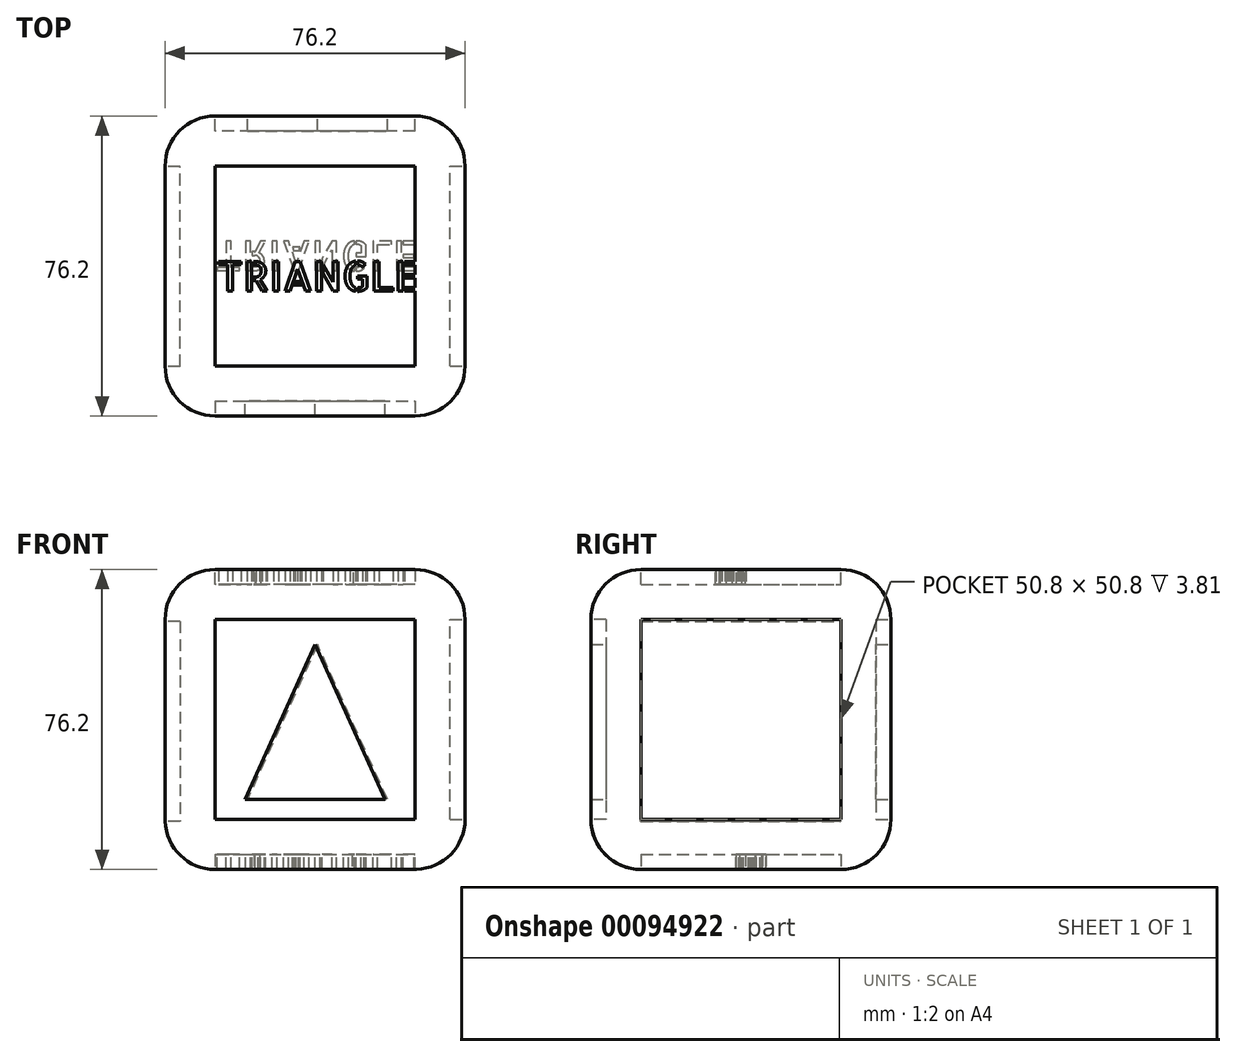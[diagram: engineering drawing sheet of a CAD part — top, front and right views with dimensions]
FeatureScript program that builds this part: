
annotation { "Feature Type Name" : "Feature", "Feature Type Description" : "" }
export const myFeature = defineFeature(function(context is Context, id is Id, definition is map)
    precondition{}
    {
        {
            var Q0;
            Q0=qCreatedBy(makeId("Front.planeOp"),FACE);
            var sketch = newSketch(context, id + "F0", { "sketchPlane" : qUnion([Q0])});
            skLineSegment(sketch, "E0", {"start": v(0, 0) * mm, "end": v(76.2, 0) * mm});
            skLineSegment(sketch, "E1", {"start": v(76.2, 0) * mm, "end": v(76.2, 76.2) * mm});
            skLineSegment(sketch, "E2", {"start": v(76.2, 76.2) * mm, "end": v(0, 76.2) * mm});
            skLineSegment(sketch, "E3", {"start": v(0, 76.2) * mm, "end": v(0, 0) * mm});
            skSolve(sketch);
        }
        {
            var Q0;
            Q0 = qSketchRegion(id + "F0", true);
            var Q1;
            Q1=makeQuery(id+"F0.imprint","IMPRINT",FACE,{"disambiguationData":[TD([[makeQuery(id+"F0.imprint","IMPRINT",EDGE,{"derivedFrom":sQuery(id+"F0.wireOp",EDGE,"E0")}),1.0]])]});
            extrude(context, id + "F1", {"entities" : qUnion([Q0, Q1]), "depth" : 76.2 * mm});
        }
        {
            var Q0;
            Q0=makeQuery(id+"F1.opExtrude","CAP_EDGE",EDGE,{"disambiguationData":[OSD([sQuery(id+"F0.wireOp",EDGE,"E1")])],"isStart":false});
            var Q1;
            Q1=makeQuery(id+"F1.opExtrude","CAP_EDGE",EDGE,{"disambiguationData":[OSD([sQuery(id+"F0.wireOp",EDGE,"E2")])],"isStart":false});
            var Q2;
            Q2=makeQuery(id+"F1.opExtrude","CAP_EDGE",EDGE,{"disambiguationData":[OSD([sQuery(id+"F0.wireOp",EDGE,"E3")])],"isStart":false});
            var Q3;
            Q3=makeQuery(id+"F1.opExtrude","CAP_EDGE",EDGE,{"disambiguationData":[OSD([sQuery(id+"F0.wireOp",EDGE,"E0")])],"isStart":false});
            var Q4;
            Q4=makeQuery(id+"F1.opExtrude","SWEPT_EDGE",EDGE,{"disambiguationData":[OSD([sQuery(id+"F0.wireOp",EDGE,"E0"),sQuery(id+"F0.wireOp",EDGE,"E1")])]});
            var Q5;
            Q5=makeQuery(id+"F1.opExtrude","SWEPT_EDGE",EDGE,{"disambiguationData":[OSD([sQuery(id+"F0.wireOp",EDGE,"E1"),sQuery(id+"F0.wireOp",EDGE,"E2")])]});
            var Q6;
            Q6=makeQuery(id+"F1.opExtrude","SWEPT_FACE",FACE,{"disambiguationData":[OSD([sQuery(id+"F0.wireOp",EDGE,"E1")])]});
            var Q7;
            Q7=makeQuery(id+"F1.opExtrude","SWEPT_EDGE",EDGE,{"disambiguationData":[OSD([sQuery(id+"F0.wireOp",EDGE,"E0"),sQuery(id+"F0.wireOp",EDGE,"E3")])]});
            var Q8;
            Q8=makeQuery(id+"F1.opExtrude","CAP_EDGE",EDGE,{"disambiguationData":[OSD([sQuery(id+"F0.wireOp",EDGE,"E0")])],"isStart":true});
            var Q9;
            Q9=makeQuery(id+"F1.opExtrude","SWEPT_FACE",FACE,{"disambiguationData":[OSD([sQuery(id+"F0.wireOp",EDGE,"E2")])]});
            var Q10;
            Q10=makeQuery(id+"F1.opExtrude","CAP_FACE",FACE,{"disambiguationData":[OSD([sQuery(id+"F0.wireOp",EDGE,"E0"),sQuery(id+"F0.wireOp",EDGE,"E1"),sQuery(id+"F0.wireOp",EDGE,"E2"),sQuery(id+"F0.wireOp",EDGE,"E3")])],"isStart":true});
            fillet(context, id + "F2", {"entities" : qUnion([Q0, Q1, Q2, Q3, Q4, Q5, Q6, Q7, Q8, Q9, Q10]), "radius" : 12.7 * mm, "tangentPropagation" : true, "allowEdgeOverflow" : false});
        }
        {
            var Q0;
            Q0=qCreatedBy(makeId("Front.planeOp"),FACE);
            var sketch = newSketch(context, id + "F3", { "sketchPlane" : qUnion([Q0])});
            skLineSegment(sketch, "E4", {"start": v(12.72, 63.63) * mm, "end": v(12.72, 12.83) * mm});
            skLineSegment(sketch, "E5", {"start": v(12.72, 12.83) * mm, "end": v(63.52, 12.83) * mm});
            skLineSegment(sketch, "E6", {"start": v(12.72, 63.63) * mm, "end": v(63.52, 63.63) * mm});
            skLineSegment(sketch, "E7", {"start": v(63.52, 63.63) * mm, "end": v(63.52, 12.83) * mm});
            skSolve(sketch);
        }
        {
            var Q0;
            Q0 = qSketchRegion(id + "F3", true);
            var Q1;
            Q1=makeQuery(id+"F1.opExtrude","CAP_FACE",FACE,{"disambiguationData":[OSD([sQuery(id+"F0.wireOp",EDGE,"E0"),sQuery(id+"F0.wireOp",EDGE,"E1"),sQuery(id+"F0.wireOp",EDGE,"E2"),sQuery(id+"F0.wireOp",EDGE,"E3")])],"isStart":false});
            extrude(context, id + "F4", {"entities" : qUnion([Q0, Q1]), "operationType" : NewBodyOperationType.REMOVE, "oppositeDirection" : true, "depth" : 3.8 * mm});
        }
        {
            var Q0;
            Q0=makeQuery(id+"F1.opExtrude","SWEPT_FACE",FACE,{"disambiguationData":[OSD([sQuery(id+"F0.wireOp",EDGE,"E1")])]});
            var sketch = newSketch(context, id + "F5", { "sketchPlane" : qUnion([Q0])});
            skLineSegment(sketch, "E8", {"start": v(-12.7, 63.5) * mm, "end": v(-63.5, 63.5) * mm});
            skLineSegment(sketch, "E9", {"start": v(-63.5, 63.5) * mm, "end": v(-63.5, 12.7) * mm});
            skLineSegment(sketch, "E10", {"start": v(-63.5, 12.7) * mm, "end": v(-12.7, 12.7) * mm});
            skLineSegment(sketch, "E11", {"start": v(-12.7, 12.7) * mm, "end": v(-12.7, 63.5) * mm});
            skSolve(sketch);
        }
        {
            var Q0;
            Q0 = qSketchRegion(id + "F5", true);
            extrude(context, id + "F6", {"entities" : qUnion([Q0]), "operationType" : NewBodyOperationType.REMOVE, "oppositeDirection" : true, "depth" : 3.8 * mm});
        }
        {
            var Q0;
            Q0=makeQuery(id+"F1.opExtrude","CAP_FACE",FACE,{"disambiguationData":[OSD([sQuery(id+"F0.wireOp",EDGE,"E0"),sQuery(id+"F0.wireOp",EDGE,"E1"),sQuery(id+"F0.wireOp",EDGE,"E2"),sQuery(id+"F0.wireOp",EDGE,"E3")])],"isStart":true});
            var sketch = newSketch(context, id + "F7", { "sketchPlane" : qUnion([Q0])});
            skLineSegment(sketch, "E12", {"start": v(-63.5, 63.5) * mm, "end": v(-12.7, 63.5) * mm});
            skLineSegment(sketch, "E13", {"start": v(-12.7, 63.5) * mm, "end": v(-12.7, 12.7) * mm});
            skLineSegment(sketch, "E14", {"start": v(-12.7, 12.7) * mm, "end": v(-63.5, 12.7) * mm});
            skLineSegment(sketch, "E15", {"start": v(-63.5, 12.7) * mm, "end": v(-63.5, 63.5) * mm});
            skSolve(sketch);
        }
        {
            var Q0;
            Q0 = qSketchRegion(id + "F7", true);
            extrude(context, id + "F8", {"entities" : qUnion([Q0]), "operationType" : NewBodyOperationType.REMOVE, "oppositeDirection" : true, "depth" : 3.8 * mm});
        }
        {
            var Q0;
            Q0=qCreatedBy(makeId("Right.planeOp"),FACE);
            var sketch = newSketch(context, id + "F9", { "sketchPlane" : qUnion([Q0])});
            skLineSegment(sketch, "E16", {"start": v(-12.83, 63.06) * mm, "end": v(-12.83, 12.26) * mm});
            skLineSegment(sketch, "E17", {"start": v(-12.83, 12.72) * mm, "end": v(-63.63, 12.72) * mm});
            skLineSegment(sketch, "E18", {"start": v(-63.63, 12.26) * mm, "end": v(-63.63, 63.06) * mm});
            skLineSegment(sketch, "E19", {"start": v(-63.63, 63.06) * mm, "end": v(-12.83, 63.06) * mm});
            skLineSegment(sketch, "E20.bottom", {"start": v(-12.83, 63.06) * mm, "end": v(-63.63, 63.06) * mm});
            skLineSegment(sketch, "E20.top", {"start": v(-12.83, 12.26) * mm, "end": v(-63.63, 12.26) * mm});
            skLineSegment(sketch, "E20.right", {"start": v(-63.63, 63.06) * mm, "end": v(-63.63, 12.26) * mm});
            skSolve(sketch);
        }
        {
            var Q0;
            Q0 = qSketchRegion(id + "F9", true);
            extrude(context, id + "F10", {"entities" : qUnion([Q0]), "operationType" : NewBodyOperationType.REMOVE, "depth" : 3.8 * mm});
        }
        {
            var Q0;
            Q0=makeQuery(id+"F1.opExtrude","SWEPT_FACE",FACE,{"disambiguationData":[OSD([sQuery(id+"F0.wireOp",EDGE,"E0")])]});
            var sketch = newSketch(context, id + "F11", { "sketchPlane" : qUnion([Q0])});
            skSolve(sketch);
        }
        {
            var Q0;
            {var subQ0=sQuery(id+"F0.wireOp",EDGE,"E0");var subQ1=makeQuery(id+"F1.opExtrude","SWEPT_FACE",FACE,{"disambiguationData":[OSD([subQ0])]});Q0=makeQuery(id+"F11.imprint","IMPRINT",FACE,{"disambiguationData":[TD([[makeQuery(id+"F11.imprint","IMPRINT",EDGE,{"derivedFrom":makeQuery(id+"F2.opFillet","BLEND_EDGE",EDGE,{"blendedFrom":[makeQuery(id+"F1.opExtrude","CAP_EDGE",EDGE,{"disambiguationData":[OSD([subQ0])],"isStart":true}),subQ1],"blendedInto":[subQ1]})}),1.0]])]});}
            extrude(context, id + "F12", {"entities" : qUnion([Q0]), "operationType" : NewBodyOperationType.REMOVE, "oppositeDirection" : true, "depth" : 3.8 * mm});
        }
        {
            var Q0;
            Q0=qCreatedBy(makeId("Top.planeOp"),FACE);
            var sketch = newSketch(context, id + "F13", { "sketchPlane" : qUnion([Q0])});
            skLineSegment(sketch, "E21", {"start": v(13.06, -12.74) * mm, "end": v(13.06, -63.54) * mm});
            skLineSegment(sketch, "E22", {"start": v(13.06, -63.54) * mm, "end": v(63.86, -63.54) * mm});
            skLineSegment(sketch, "E23", {"start": v(63.86, -63.54) * mm, "end": v(63.86, -12.74) * mm});
            skLineSegment(sketch, "E24", {"start": v(63.86, -12.74) * mm, "end": v(13.06, -12.74) * mm});
            skSolve(sketch);
        }
        {
            var Q0;
            Q0 = qSketchRegion(id + "F13", true);
            var Q1;
            Q1=makeQuery(id+"F1.opExtrude","SWEPT_FACE",FACE,{"disambiguationData":[OSD([sQuery(id+"F0.wireOp",EDGE,"E2")])]});
            extrude(context, id + "F14", {"entities" : qUnion([Q0, Q1]), "operationType" : NewBodyOperationType.REMOVE, "oppositeDirection" : true, "depth" : 3.8 * mm});
        }
        {
            var Q0;
            Q0=qCreatedBy(makeId("Front.planeOp"),FACE);
            var sketch = newSketch(context, id + "F15", { "sketchPlane" : qUnion([Q0])});
            skLineSegment(sketch, "E25", {"start": v(38.69, 57.13) * mm, "end": v(20.9, 17.78) * mm});
            skLineSegment(sketch, "E26", {"start": v(20.9, 17.78) * mm, "end": v(56.47, 17.78) * mm});
            skLineSegment(sketch, "E27", {"start": v(56.47, 17.78) * mm, "end": v(38.69, 57.13) * mm});
            skSolve(sketch);
        }
        {
            var Q0;
            Q0=makeQuery(id+"F15.imprint","IMPRINT",FACE,{"disambiguationData":[TD([[makeQuery(id+"F15.imprint","IMPRINT",EDGE,{"derivedFrom":sQuery(id+"F15.wireOp",EDGE,"E25")}),1.0]])]});
            extrude(context, id + "F16", {"entities" : qUnion([Q0]), "operationType" : NewBodyOperationType.ADD, "depth" : 25.4 * mm});
        }
        {
            var Q0;
            Q0=makeQuery(id+"F4.boolean.opBoolean","COPY",FACE,{"derivedFrom":makeQuery(id+"F4.opExtrude","CAP_FACE",FACE,{"disambiguationData":[OSD([sQuery(id+"F0.wireOp",EDGE,"E0"),sQuery(id+"F0.wireOp",EDGE,"E1"),sQuery(id+"F0.wireOp",EDGE,"E2"),sQuery(id+"F0.wireOp",EDGE,"E3")])],"isStart":false})});
            var sketch = newSketch(context, id + "F17", { "sketchPlane" : qUnion([Q0])});
            skLineSegment(sketch, "E28", {"start": v(38.1, 57.13) * mm, "end": v(20.32, 17.78) * mm});
            skLineSegment(sketch, "E29", {"start": v(20.32, 17.78) * mm, "end": v(55.88, 17.78) * mm});
            skLineSegment(sketch, "E30", {"start": v(55.88, 17.78) * mm, "end": v(38.1, 57.13) * mm});
            skPoint(sketch, "E31", {"position": v(38.1, 17.78) * mm});
            skLineSegment(sketch, "E32", {"start": v(12.7, 12.7) * mm, "end": v(63.5, 12.7) * mm});
            skPoint(sketch, "E33", {"position": v(38.1, 12.7) * mm});
            skSolve(sketch);
        }
        {
            var Q0;
            Q0 = qSketchRegion(id + "F17", true);
            extrude(context, id + "F18", {"entities" : qUnion([Q0]), "operationType" : NewBodyOperationType.ADD, "depth" : 3.8 * mm});
        }
        {
            var Q0;
            Q0=makeQuery(id+"F14.boolean.opBoolean","COPY",FACE,{"derivedFrom":makeQuery(id+"F14.opExtrude","CAP_FACE",FACE,{"disambiguationData":[OSD([sQuery(id+"F0.wireOp",EDGE,"E2")])],"isStart":false})});
            var sketch = newSketch(context, id + "F19", { "sketchPlane" : qUnion([Q0])});
            skText(sketch, "E34", { "text": "TRIANGLE", "fontName": "AllertaStencil-Regular.ttf"});
            const initialGuessF19  = {"E34": [0.01306, -0.04449, 1, 0, 0.00756]};
            skSetInitialGuess(sketch, initialGuessF19);
            skSolve(sketch);
        }
        {
            var Q0;
            Q0 = qSketchRegion(id + "F19", true);
            extrude(context, id + "F20", {"entities" : qUnion([Q0]), "operationType" : NewBodyOperationType.ADD, "depth" : 3.8 * mm});
        }
        {
            var Q0;
            Q0=makeQuery(id+"F12.boolean.opBoolean","COPY",FACE,{"derivedFrom":makeQuery(id+"F12.opExtrude","CAP_FACE",FACE,{"disambiguationData":[OSD([sQuery(id+"F0.wireOp",EDGE,"E0"),sQuery(id+"F0.wireOp",EDGE,"E1"),sQuery(id+"F0.wireOp",EDGE,"E3")])],"isStart":false})});
            var sketch = newSketch(context, id + "F21", { "sketchPlane" : qUnion([Q0])});
            skText(sketch, "E35", { "text": "TRIANGLE", "fontName": "AllertaStencil-Regular.ttf"});
            const initialGuessF21  = {"E35": [0.0127, 0.03175, 1, 0, 0.00756]};
            skSetInitialGuess(sketch, initialGuessF21);
            skSolve(sketch);
        }
        {
            var Q0;
            Q0 = qSketchRegion(id + "F21", true);
            extrude(context, id + "F22", {"entities" : qUnion([Q0]), "operationType" : NewBodyOperationType.ADD, "depth" : 3.8 * mm});
        }
    });
